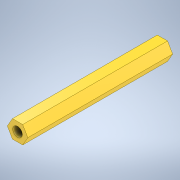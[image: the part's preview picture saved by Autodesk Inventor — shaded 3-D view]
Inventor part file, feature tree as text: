
AUTODESK INVENTOR PART (.ipt)
format: ipt  version: 2020 (Build 240168000, 168)  size: 100,352 bytes
history: native  units: mm
features: extrude x1, sketch x1
ambient origin geometry x8: Origin, YZ Plane, XZ Plane, XY Plane, X Axis, Y Axis, Z Axis, Center Point
bodies: Solid1 (feature_tree)
feature tree (2):
  extrude  "Extrusion1"  Depth=45.0mm
  sketch  "Sketch1"  dims[d0=5.5mm d1=3.0mm d2=45.0mm d3=0.0mm]
